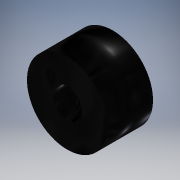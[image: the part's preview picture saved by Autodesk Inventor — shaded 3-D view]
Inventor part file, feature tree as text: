
AUTODESK INVENTOR PART (.ipt)
format: ipt  version: 2019.4 (Build 234330000, 330)  size: 98,816 bytes
history: native  units: mm
features: extrude x1, sketch x1
ambient origin geometry x8: Origin, YZ Plane, XZ Plane, XY Plane, X Axis, Y Axis, Z Axis, Center Point
bodies: Volumenkörper1 (feature_tree)
feature tree (2):
  extrude  "Extrusion1"  Depth=4.4mm TaperAngle=0.0deg
  sketch  "Skizze1"  dims[d0=7.8mm d1=4.4mm d2=0.0mm]
